FCSTD DOCUMENT  (FreeCAD 0.19R0.19.2)
Label: boatMoterHolder003
License: All rights reserved
LicenseURL: http://en.wikipedia.org/wiki/All_rights_reserved
objects: Sketcher::SketchObject×1
note: 1 computed .brp shape members not serialized (recipe doc carries the construction recipe); baked Part::Feature solids carry a one-line shape summary decoded from their .brp

FEATURE [Sketcher::SketchObject] Sketch
  FullyConstrained = false
  sketch-geometry (32):
    g0: Circle CenterX=-6 CenterY=0 CenterZ=0 NormalX=0 NormalY=0 NormalZ=1 AngleXU=0 Radius=0.9
    g1: Circle CenterX=0 CenterY=6 CenterZ=0 NormalX=0 NormalY=0 NormalZ=1 AngleXU=0 Radius=0.9
    g2: Circle CenterX=6 CenterY=0 CenterZ=0 NormalX=0 NormalY=0 NormalZ=1 AngleXU=0 Radius=0.9
    g3: Circle CenterX=0 CenterY=-6 CenterZ=0 NormalX=0 NormalY=0 NormalZ=1 AngleXU=0 Radius=0.9
    g4: LineSegment StartX=0 StartY=0 StartZ=0 EndX=3.53553 EndY=-3.53553 EndZ=0
    g5: LineSegment StartX=-3.53553 StartY=-3.53553 StartZ=0 EndX=0 EndY=0 EndZ=0
    g6: LineSegment StartX=3.53553 StartY=3.53553 StartZ=0 EndX=-4e-16 EndY=0 EndZ=0
    g7: LineSegment StartX=0 StartY=0 StartZ=0 EndX=-3.53553 EndY=3.53553 EndZ=0
    g8: LineSegment StartX=-7.77817 StartY=7.77817 StartZ=0 EndX=-3.53553 EndY=3.53553 EndZ=0
    g9: LineSegment StartX=3.53553 StartY=-3.53553 StartZ=0 EndX=7.77817 EndY=-7.77817 EndZ=0
    g10: LineSegment StartX=3.53553 StartY=3.53553 StartZ=0 EndX=7.77817 EndY=7.77817 EndZ=0
    g11: LineSegment StartX=-3.53553 StartY=-3.53553 StartZ=0 EndX=-7.77817 EndY=-7.77817 EndZ=0
    g12: LineSegment StartX=3.53553 StartY=-3.53553 StartZ=0 EndX=4.94975 EndY=-4.94975 EndZ=0
    g13: LineSegment StartX=-3.53553 StartY=-3.53553 StartZ=0 EndX=-4.94975 EndY=-4.94975 EndZ=0
    g14: LineSegment StartX=-3.53553 StartY=3.53553 StartZ=0 EndX=-4.94975 EndY=4.94975 EndZ=0
    g15: LineSegment StartX=3.53553 StartY=3.53553 StartZ=0 EndX=4.94975 EndY=4.94975 EndZ=0
    g16: LineSegment StartX=4.94975 StartY=4.94975 StartZ=0 EndX=6.36396 EndY=3.53553 EndZ=0
    g17: LineSegment StartX=-4.94975 StartY=-4.94975 StartZ=0 EndX=-3.50877 EndY=-6.33668 EndZ=0
    g18: LineSegment StartX=-4.94975 StartY=4.94975 StartZ=0 EndX=-3.53553 EndY=6.36396 EndZ=0
    g19: LineSegment StartX=4.94975 StartY=-4.94975 StartZ=0 EndX=6.34846 EndY=-3.5202 EndZ=0
    g20: LineSegment StartX=4.94975 StartY=4.94975 StartZ=0 EndX=3.53553 EndY=6.36396 EndZ=0
    g21: LineSegment StartX=-4.94975 StartY=-4.94975 StartZ=0 EndX=-6.36281 EndY=-3.53439 EndZ=0
    g22: LineSegment StartX=-4.94975 StartY=4.94975 StartZ=0 EndX=-6.36396 EndY=3.53553 EndZ=0
    g23: LineSegment StartX=4.94975 StartY=-4.94975 StartZ=0 EndX=3.53551 EndY=-6.36394 EndZ=0
    g24: LineSegment StartX=7.77817 StartY=7.77817 StartZ=0 EndX=10.6066 EndY=4.94975 EndZ=0
    g25: LineSegment StartX=-7.77817 StartY=-7.77817 StartZ=0 EndX=-4.92861 EndY=-10.5853 EndZ=0
    g26: LineSegment StartX=7.77817 StartY=7.77817 StartZ=0 EndX=4.94975 EndY=10.6066 EndZ=0
    g27: LineSegment StartX=-7.77817 StartY=-7.77817 StartZ=0 EndX=-10.6066 EndY=-4.94975 EndZ=0
    g28: LineSegment StartX=-7.77817 StartY=7.77817 StartZ=0 EndX=-4.94975 EndY=10.6066 EndZ=0
    g29: LineSegment StartX=7.77817 StartY=-7.77817 StartZ=0 EndX=10.6239 EndY=-4.96711 EndZ=0
    g30: LineSegment StartX=-7.77817 StartY=7.77817 StartZ=0 EndX=-10.6066 EndY=4.94975 EndZ=0
    g31: LineSegment StartX=7.77817 StartY=-7.77817 StartZ=0 EndX=4.94975 EndY=-10.6066 EndZ=0
  constraints (80):
    c: Block(g1)
    c: Block(g2)
    c: Block(g3)
    c: Block(g0)
    c: Coincident(g4,g-1)
    c: Distance(g4) = 5
    c: Angle(g4,g-1) = 0.785398
    c: Equal(g4,g5) = 5
    c: Coincident(g5,g4)
    c: Angle(g6,g-1) = 2.35619
    c: Distance(g6) = 5
    c: Coincident(g6,g4)
    c: Angle(g-1,g5) = 3.92699
    c: Coincident(g7,g4)
    c: Angle(g7,g5) = 1.5708
    c: Distance(g7) = 5
    c: Coincident(g8,g7)
    c: Distance(g8) = 6
    c: Parallel(g7,g8)
    c: Coincident(g9,g4)
    c: Distance(g9) = 6
    c: Parallel(g9,g4)
    c: Coincident(g10,g6)
    c: Distance(g10) = 6
    c: Parallel(g10,g6)
    c: Coincident(g11,g5)
    c: Distance(g11) = 6
    c: Parallel(g11,g5)
    c: Coincident(g12,g4)
    c: Distance(g12) = 2
    c: Coincident(g13,g5)
    c: Distance(g13) = 2
    c: Coincident(g14,g7)
    c: Distance(g14) = 2
    c: Coincident(g15,g6)
    c: Distance(g15) = 2
    c: Parallel(g15,g10)
    c: Parallel(g12,g9)
    c: Parallel(g13,g11)
    c: Parallel(g14,g8)
    c: Distance(g16) = 2
    c: Perpendicular(g10,g16)
    c: Coincident(g16,g15)
    c: Equal(g16,g17) = 2
    c: Coincident(g17,g13)
    c: Coincident(g18,g14)
    c: Distance(g18) = 2
    c: Perpendicular(g8,g18)
    c: Equal(g18,g19) = 2
    c: Coincident(g19,g12)
    c: Coincident(g20,g15)
    c: Distance(g20) = 2
    c: Perpendicular(g10,g20)
    c: Equal(g20,g21) = 2
    c: Coincident(g21,g13)
    c: Coincident(g22,g14)
    c: Distance(g22) = 2
    c: Perpendicular(g8,g22)
    c: Equal(g22,g23) = 2
    c: Coincident(g23,g12)
    c: Distance(g24) = 4
    c: Perpendicular(g10,g24)
    c: Coincident(g24,g10)
    c: Equal(g24,g25) = 4
    c: Coincident(g25,g11)
    c: Coincident(g26,g10)
    c: Distance(g26) = 4
    c: Perpendicular(g10,g26)
    c: Equal(g26,g27) = 4
    c: Coincident(g27,g11)
    c: Coincident(g28,g8)
    c: Distance(g28) = 4
    c: Perpendicular(g8,g28)
    c: Equal(g28,g29) = 4
    c: Coincident(g29,g9)
    c: Coincident(g30,g8)
    c: Distance(g30) = 4
    c: Perpendicular(g30,g8)
    c: Equal(g30,g31) = 4
    c: Coincident(g31,g9)
